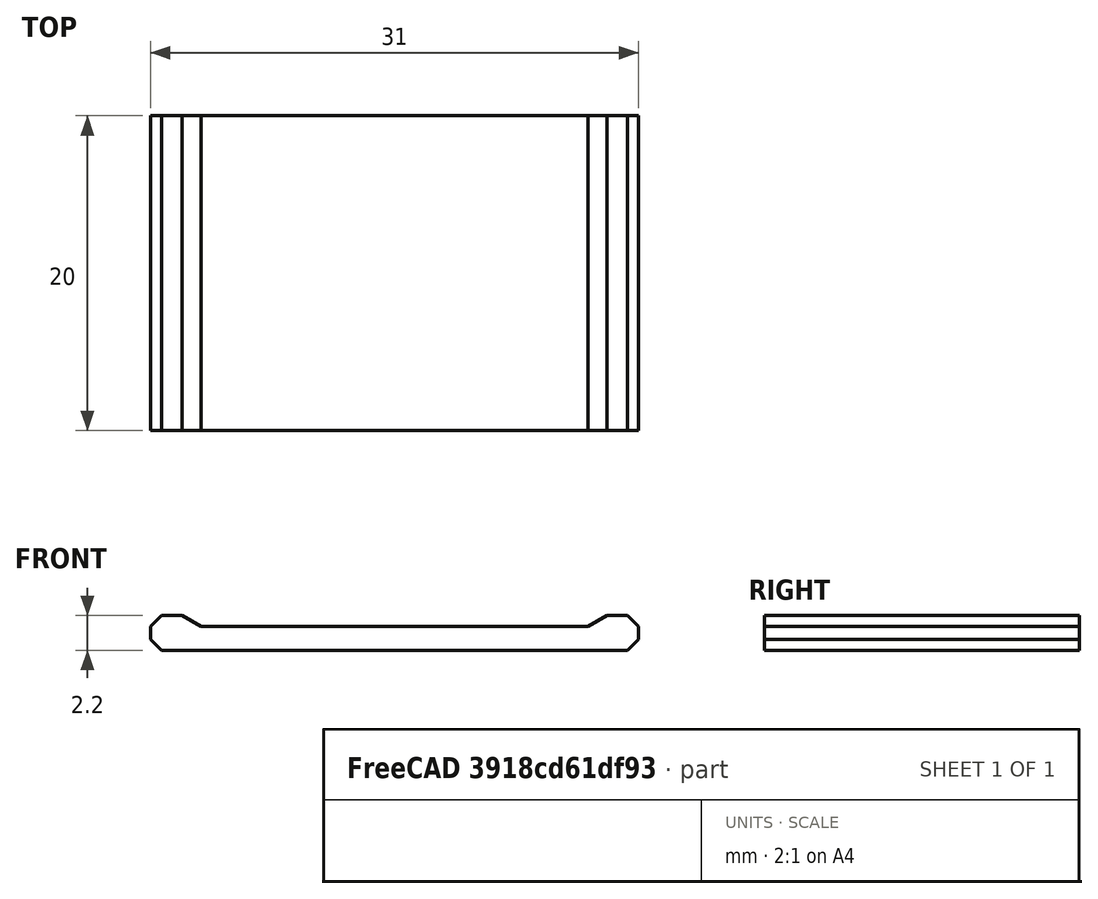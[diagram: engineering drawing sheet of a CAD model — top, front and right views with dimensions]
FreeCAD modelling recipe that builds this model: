
FCSTD DOCUMENT  (FreeCAD 0.21R33771 (Git))
Label: 3DFDM_Attachment_tool
License: All rights reserved
LicenseURL: https://en.wikipedia.org/wiki/All_rights_reserved
objects: Sketcher::SketchObject×1, PartDesign::Pad×1, PartDesign::Body×1
note: 4 computed .brp shape members not serialized (recipe doc carries the construction recipe); baked Part::Feature solids carry a one-line shape summary decoded from their .brp

FEATURE [Sketcher::SketchObject] Sketch019
  FullyConstrained = true
  MapMode = 5
  Placement = pos=(0,0,0) rot=(1,0,0;1.5708rad)
  Support = -> [XZ_Plane001]
  sketch-geometry (16):
    g0: LineSegment StartX=-39.7624 StartY=-1e-16 StartZ=0 EndX=-38.55 EndY=0.7 EndZ=0
    g1: LineSegment StartX=-38.55 StartY=0.7 StartZ=0 EndX=-37.25 EndY=0.7 EndZ=0
    g2: LineSegment StartX=-36.55 StartY=-1e-16 StartZ=0 EndX=-36.55 EndY=-0.8 EndZ=0
    g3: LineSegment StartX=-37.25 StartY=-1.5 StartZ=0 EndX=-66.85 EndY=-1.5 EndZ=0
    g4: GeomPoint X=-52.05 Y=1.5 Z=0
    g5: LineSegment StartX=-39.7624 StartY=-1e-16 StartZ=0 EndX=-64.3376 EndY=-1e-16 EndZ=0
    g6: LineSegment StartX=-52.05 StartY=1.5 StartZ=0 EndX=-52.05 EndY=-1.5 EndZ=0
    g7: LineSegment StartX=-64.3376 StartY=-1e-16 StartZ=0 EndX=-65.55 EndY=0.7 EndZ=0
    g8: LineSegment StartX=-65.55 StartY=0.7 StartZ=0 EndX=-66.85 EndY=0.7 EndZ=0
    g9: LineSegment StartX=-67.55 StartY=-1e-16 StartZ=0 EndX=-67.55 EndY=-0.8 EndZ=0
    g10: LineSegment StartX=-37.25 StartY=0.7 StartZ=0 EndX=-36.55 EndY=-1e-16 EndZ=0
    g11: LineSegment StartX=-36.55 StartY=-0.8 StartZ=0 EndX=-37.25 EndY=-1.5 EndZ=0
    g12: LineSegment StartX=-66.85 StartY=0.7 StartZ=0 EndX=-67.55 EndY=-1e-16 EndZ=0
    g13: LineSegment StartX=-67.55 StartY=-0.8 StartZ=0 EndX=-66.85 EndY=-1.5 EndZ=0
    g14: GeomPoint X=-52.05 Y=-0.75 Z=0
    g15: GeomPoint X=-52.05 Y=-1e-16 Z=0
  constraints (40):
    c: Coincident(g1,g0)
    c: Horizontal(g1)
    c: Horizontal(g3)
    c: Vertical(g2)
    c: DistanceY(g-1,g4) = 1.5
    c: DistanceY(g0,g0) = 0.7
    c: Coincident(g5,g0)
    c: Horizontal(g5)
    c: Angle(g0,g5) = 2.61799
    c: DistanceX(g4,g-1) = 52.05
    c: Coincident(g6,g4)
    c: Symmetric(g5,g0,g6)
    c: Coincident(g7,g5)
    c: Coincident(g8,g7)
    c: Horizontal(g8)
    c: Vertical(g9)
    c: DistanceY(g10,g10) = 0.7
    c: Angle(g10,g2) = 2.35619
    c: DistanceY(g11,g11) = 0.7
    c: Angle(g11,g3) = 2.35619
    c: Coincident(g1,g10)
    c: Coincident(g2,g10)
    c: Coincident(g2,g11)
    c: Coincident(g3,g11)
    c: DistanceX(g4,g2) = 15.5
    c: Coincident(g9,g13)
    c: Coincident(g3,g13)
    c: Coincident(g9,g12)
    c: Coincident(g8,g12)
    c: Equal(g8,g1)
    c: Equal(g9,g2)
    c: Symmetric(g3,g3,g6)
    c: Symmetric(g9,g2,g6)
    c: Symmetric(g8,g1,g6)
    c: DistanceX(g4,g0) = 13.5
    c: DistanceY(g3,g0) = 1.5
    c: PointOnObject(g14,g6)
    c: PointOnObject(g15,g5)
    c: Symmetric(g15,g6,g14)
    c: DistanceY(g14,g4) = 2.25
FEATURE [PartDesign::Pad] Pad006
  Direction = (0,-1,-2e-16)
  Length = 20
  Length2 = 10
  Midplane = true
  Placement = pos=(0,0,0) rot=(1,0,0;1.5708rad)
  Profile = -> Sketch019
  ReferenceAxis = -> Sketch019 [N_Axis]
  Type = 0
FEATURE [PartDesign::Body] Body001  label="3DFDM_Attachment_tool"
  Group = -> [Sketch019,Pad006]
  Origin = -> Origin001
  Tip = -> Pad006
